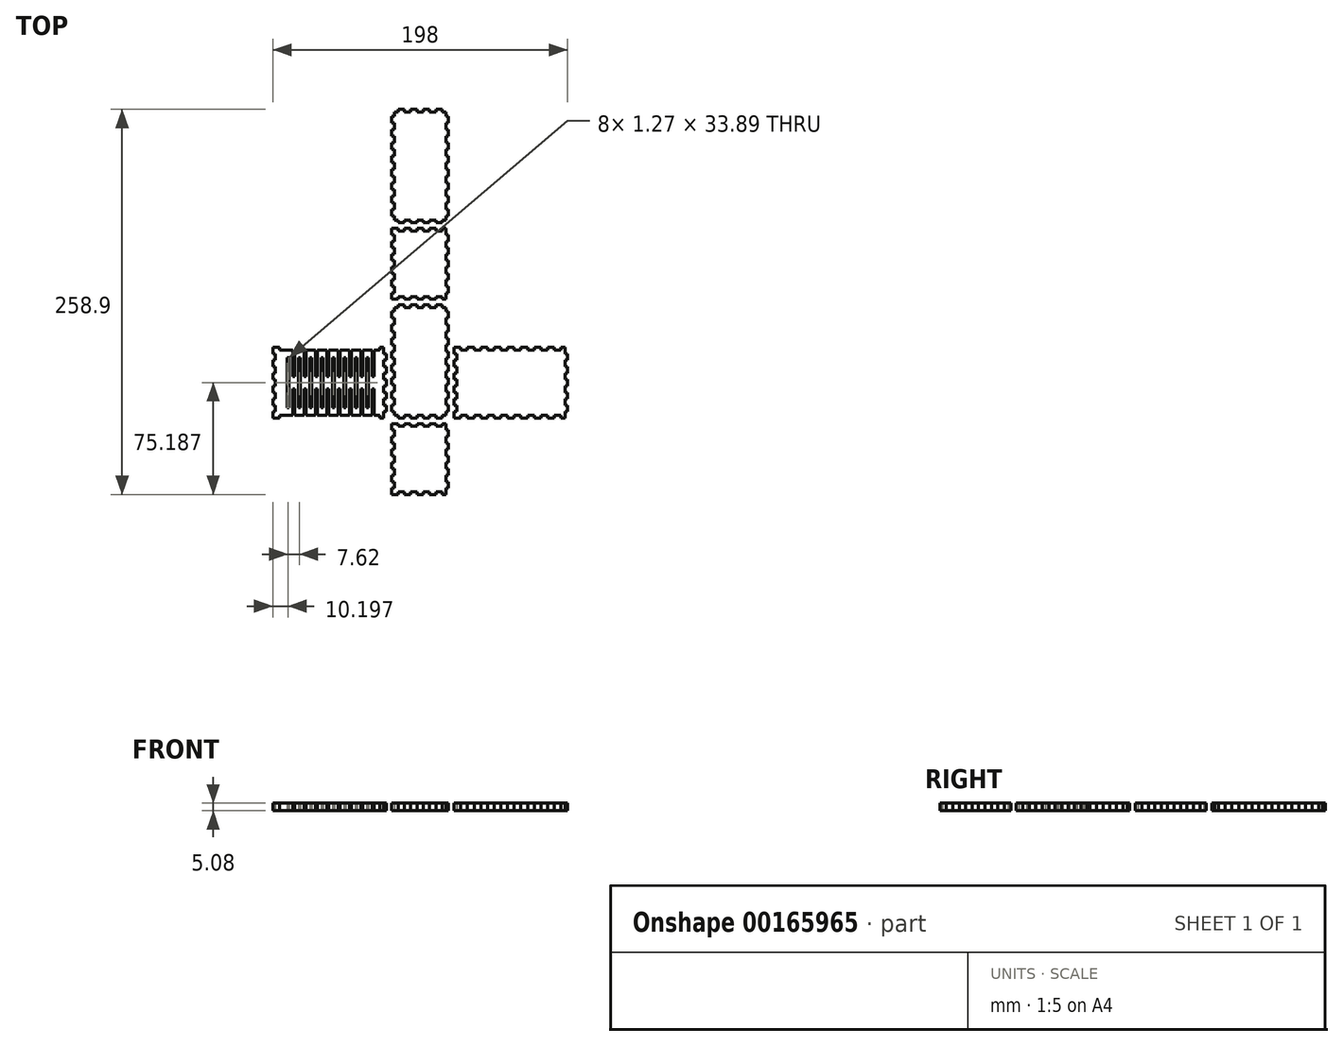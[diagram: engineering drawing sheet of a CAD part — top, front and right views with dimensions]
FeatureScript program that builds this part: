
annotation { "Feature Type Name" : "Feature", "Feature Type Description" : "" }
export const myFeature = defineFeature(function(context is Context, id is Id, definition is map)
    precondition{}
    {
        {
            var Q0;
            Q0=qCreatedBy(makeId("Top.planeOp"),FACE);
            var sketch = newSketch(context, id + "F0", { "sketchPlane" : qUnion([Q0])});
            skLineSegment(sketch, "E0", {"start": v(-19.05, -129.45) * mm, "end": v(-14.82, -129.45) * mm});
            skLineSegment(sketch, "E1", {"start": v(-14.82, -127.66) * mm, "end": v(-14.82, -129.45) * mm});
            skLineSegment(sketch, "E2", {"start": v(-14.82, -127.66) * mm, "end": v(-10.58, -127.66) * mm});
            skLineSegment(sketch, "E3", {"start": v(-10.58, -127.66) * mm, "end": v(-10.58, -129.45) * mm});
            skLineSegment(sketch, "E4", {"start": v(-10.58, -129.45) * mm, "end": v(-6.35, -129.45) * mm});
            skLineSegment(sketch, "E5", {"start": v(-6.35, -127.66) * mm, "end": v(-6.35, -129.45) * mm});
            skLineSegment(sketch, "E6", {"start": v(-6.35, -127.66) * mm, "end": v(-2.12, -127.66) * mm});
            skLineSegment(sketch, "E7", {"start": v(-2.12, -127.66) * mm, "end": v(-2.12, -129.45) * mm});
            skLineSegment(sketch, "E8", {"start": v(-2.12, -129.45) * mm, "end": v(2.12, -129.45) * mm});
            skLineSegment(sketch, "E9", {"start": v(2.12, -127.66) * mm, "end": v(2.12, -129.45) * mm});
            skLineSegment(sketch, "E10", {"start": v(2.12, -127.66) * mm, "end": v(6.35, -127.66) * mm});
            skLineSegment(sketch, "E11", {"start": v(6.35, -127.66) * mm, "end": v(6.35, -129.45) * mm});
            skLineSegment(sketch, "E12", {"start": v(6.35, -129.45) * mm, "end": v(10.58, -129.45) * mm});
            skLineSegment(sketch, "E13", {"start": v(10.58, -127.66) * mm, "end": v(10.58, -129.45) * mm});
            skLineSegment(sketch, "E14", {"start": v(10.58, -127.66) * mm, "end": v(14.82, -127.66) * mm});
            skLineSegment(sketch, "E15", {"start": v(14.82, -127.66) * mm, "end": v(14.82, -129.45) * mm});
            skLineSegment(sketch, "E16", {"start": v(14.82, -129.45) * mm, "end": v(17.26, -129.45) * mm});
            skLineSegment(sketch, "E17", {"start": v(-19.05, -81.83) * mm, "end": v(-14.82, -81.83) * mm});
            skLineSegment(sketch, "E18", {"start": v(-14.82, -81.83) * mm, "end": v(-14.82, -83.61) * mm});
            skLineSegment(sketch, "E19", {"start": v(-14.82, -83.61) * mm, "end": v(-10.58, -83.61) * mm});
            skLineSegment(sketch, "E20", {"start": v(-10.58, -81.83) * mm, "end": v(-10.58, -83.61) * mm});
            skLineSegment(sketch, "E21", {"start": v(-10.58, -81.83) * mm, "end": v(-6.35, -81.83) * mm});
            skLineSegment(sketch, "E22", {"start": v(-6.35, -81.83) * mm, "end": v(-6.35, -83.61) * mm});
            skLineSegment(sketch, "E23", {"start": v(-6.35, -83.61) * mm, "end": v(-2.12, -83.61) * mm});
            skLineSegment(sketch, "E24", {"start": v(-2.12, -81.83) * mm, "end": v(-2.12, -83.61) * mm});
            skLineSegment(sketch, "E25", {"start": v(-2.12, -81.83) * mm, "end": v(2.12, -81.83) * mm});
            skLineSegment(sketch, "E26", {"start": v(2.12, -81.83) * mm, "end": v(2.12, -83.61) * mm});
            skLineSegment(sketch, "E27", {"start": v(2.12, -83.61) * mm, "end": v(6.35, -83.61) * mm});
            skLineSegment(sketch, "E28", {"start": v(6.35, -81.83) * mm, "end": v(6.35, -83.61) * mm});
            skLineSegment(sketch, "E29", {"start": v(6.35, -81.83) * mm, "end": v(10.58, -81.83) * mm});
            skLineSegment(sketch, "E30", {"start": v(10.58, -81.83) * mm, "end": v(10.58, -83.61) * mm});
            skLineSegment(sketch, "E31", {"start": v(10.58, -83.61) * mm, "end": v(14.82, -83.61) * mm});
            skLineSegment(sketch, "E32", {"start": v(14.82, -81.83) * mm, "end": v(14.82, -83.61) * mm});
            skLineSegment(sketch, "E33", {"start": v(14.82, -81.83) * mm, "end": v(17.26, -81.83) * mm});
            skLineSegment(sketch, "E34", {"start": v(-19.05, -129.45) * mm, "end": v(-19.05, -125.12) * mm});
            skLineSegment(sketch, "E35", {"start": v(-17.26, -125.12) * mm, "end": v(-19.05, -125.12) * mm});
            skLineSegment(sketch, "E36", {"start": v(-17.26, -125.12) * mm, "end": v(-17.26, -120.8) * mm});
            skLineSegment(sketch, "E37", {"start": v(-17.26, -120.8) * mm, "end": v(-19.05, -120.8) * mm});
            skLineSegment(sketch, "E38", {"start": v(-19.05, -120.8) * mm, "end": v(-19.05, -116.46) * mm});
            skLineSegment(sketch, "E39", {"start": v(-17.26, -116.46) * mm, "end": v(-19.05, -116.46) * mm});
            skLineSegment(sketch, "E40", {"start": v(-17.26, -116.46) * mm, "end": v(-17.26, -112.13) * mm});
            skLineSegment(sketch, "E41", {"start": v(-17.26, -112.13) * mm, "end": v(-19.05, -112.13) * mm});
            skLineSegment(sketch, "E42", {"start": v(-19.05, -112.13) * mm, "end": v(-19.05, -107.8) * mm});
            skLineSegment(sketch, "E43", {"start": v(-17.26, -107.8) * mm, "end": v(-19.05, -107.8) * mm});
            skLineSegment(sketch, "E44", {"start": v(-17.26, -107.8) * mm, "end": v(-17.26, -103.47) * mm});
            skLineSegment(sketch, "E45", {"start": v(-17.26, -103.47) * mm, "end": v(-19.05, -103.47) * mm});
            skLineSegment(sketch, "E46", {"start": v(-19.05, -103.47) * mm, "end": v(-19.05, -99.14) * mm});
            skLineSegment(sketch, "E47", {"start": v(-17.26, -99.14) * mm, "end": v(-19.05, -99.14) * mm});
            skLineSegment(sketch, "E48", {"start": v(-17.26, -99.14) * mm, "end": v(-17.26, -94.81) * mm});
            skLineSegment(sketch, "E49", {"start": v(-17.26, -94.81) * mm, "end": v(-19.05, -94.81) * mm});
            skLineSegment(sketch, "E50", {"start": v(-19.05, -94.81) * mm, "end": v(-19.05, -90.48) * mm});
            skLineSegment(sketch, "E51", {"start": v(-17.26, -90.48) * mm, "end": v(-19.05, -90.48) * mm});
            skLineSegment(sketch, "E52", {"start": v(-17.26, -90.48) * mm, "end": v(-17.26, -86.15) * mm});
            skLineSegment(sketch, "E53", {"start": v(-17.26, -86.15) * mm, "end": v(-19.05, -86.15) * mm});
            skLineSegment(sketch, "E54", {"start": v(-19.05, -86.15) * mm, "end": v(-19.05, -81.83) * mm});
            skLineSegment(sketch, "E55", {"start": v(17.26, -129.45) * mm, "end": v(17.26, -125.12) * mm});
            skLineSegment(sketch, "E56", {"start": v(19.05, -125.12) * mm, "end": v(17.26, -125.12) * mm});
            skLineSegment(sketch, "E57", {"start": v(19.05, -125.12) * mm, "end": v(19.05, -120.8) * mm});
            skLineSegment(sketch, "E58", {"start": v(19.05, -120.8) * mm, "end": v(17.26, -120.8) * mm});
            skLineSegment(sketch, "E59", {"start": v(17.26, -120.8) * mm, "end": v(17.26, -116.46) * mm});
            skLineSegment(sketch, "E60", {"start": v(19.05, -116.46) * mm, "end": v(17.26, -116.46) * mm});
            skLineSegment(sketch, "E61", {"start": v(19.05, -116.46) * mm, "end": v(19.05, -112.13) * mm});
            skLineSegment(sketch, "E62", {"start": v(19.05, -112.13) * mm, "end": v(17.26, -112.13) * mm});
            skLineSegment(sketch, "E63", {"start": v(17.26, -112.13) * mm, "end": v(17.26, -107.8) * mm});
            skLineSegment(sketch, "E64", {"start": v(19.05, -107.8) * mm, "end": v(17.26, -107.8) * mm});
            skLineSegment(sketch, "E65", {"start": v(19.05, -107.8) * mm, "end": v(19.05, -103.47) * mm});
            skLineSegment(sketch, "E66", {"start": v(19.05, -103.47) * mm, "end": v(17.26, -103.47) * mm});
            skLineSegment(sketch, "E67", {"start": v(17.26, -103.47) * mm, "end": v(17.26, -99.14) * mm});
            skLineSegment(sketch, "E68", {"start": v(19.05, -99.14) * mm, "end": v(17.26, -99.14) * mm});
            skLineSegment(sketch, "E69", {"start": v(19.05, -99.14) * mm, "end": v(19.05, -94.81) * mm});
            skLineSegment(sketch, "E70", {"start": v(19.05, -94.81) * mm, "end": v(17.26, -94.81) * mm});
            skLineSegment(sketch, "E71", {"start": v(17.26, -94.81) * mm, "end": v(17.26, -90.48) * mm});
            skLineSegment(sketch, "E72", {"start": v(19.05, -90.48) * mm, "end": v(17.26, -90.48) * mm});
            skLineSegment(sketch, "E73", {"start": v(19.05, -90.48) * mm, "end": v(19.05, -86.15) * mm});
            skLineSegment(sketch, "E74", {"start": v(19.05, -86.15) * mm, "end": v(17.26, -86.15) * mm});
            skLineSegment(sketch, "E75", {"start": v(17.26, -86.15) * mm, "end": v(17.26, -81.83) * mm});
            skLineSegment(sketch, "E76", {"start": v(-99, -78.08) * mm, "end": v(-94.52, -78.08) * mm});
            skLineSegment(sketch, "E77", {"start": v(-94.52, -76.29) * mm, "end": v(-94.52, -78.08) * mm});
            skLineSegment(sketch, "E78", {"start": v(-94.52, -76.29) * mm, "end": v(-85.63, -76.29) * mm});
            skLineSegment(sketch, "E79", {"start": v(-27.28, -76.29) * mm, "end": v(-27.28, -78.08) * mm});
            skLineSegment(sketch, "E80", {"start": v(-27.28, -78.08) * mm, "end": v(-24.59, -78.08) * mm});
            skLineSegment(sketch, "E81", {"start": v(-99, -30.45) * mm, "end": v(-94.52, -30.45) * mm});
            skLineSegment(sketch, "E82", {"start": v(-94.52, -30.45) * mm, "end": v(-94.52, -32.24) * mm});
            skLineSegment(sketch, "E83", {"start": v(-27.28, -30.45) * mm, "end": v(-27.28, -32.24) * mm});
            skLineSegment(sketch, "E84", {"start": v(-27.28, -30.45) * mm, "end": v(-24.59, -30.45) * mm});
            skLineSegment(sketch, "E85", {"start": v(-99, -78.08) * mm, "end": v(-99, -73.75) * mm});
            skLineSegment(sketch, "E86", {"start": v(-97.21, -73.75) * mm, "end": v(-99, -73.75) * mm});
            skLineSegment(sketch, "E87", {"start": v(-97.21, -73.75) * mm, "end": v(-97.21, -69.42) * mm});
            skLineSegment(sketch, "E88", {"start": v(-97.21, -69.42) * mm, "end": v(-99, -69.42) * mm});
            skLineSegment(sketch, "E89", {"start": v(-99, -69.42) * mm, "end": v(-99, -65.09) * mm});
            skLineSegment(sketch, "E90", {"start": v(-97.21, -65.09) * mm, "end": v(-99, -65.09) * mm});
            skLineSegment(sketch, "E91", {"start": v(-97.21, -65.09) * mm, "end": v(-97.21, -60.76) * mm});
            skLineSegment(sketch, "E92", {"start": v(-97.21, -60.76) * mm, "end": v(-99, -60.76) * mm});
            skLineSegment(sketch, "E93", {"start": v(-99, -60.76) * mm, "end": v(-99, -56.43) * mm});
            skLineSegment(sketch, "E94", {"start": v(-97.21, -56.43) * mm, "end": v(-99, -56.43) * mm});
            skLineSegment(sketch, "E95", {"start": v(-97.21, -56.43) * mm, "end": v(-97.21, -52.1) * mm});
            skLineSegment(sketch, "E96", {"start": v(-97.21, -52.1) * mm, "end": v(-99, -52.1) * mm});
            skLineSegment(sketch, "E97", {"start": v(-99, -52.1) * mm, "end": v(-99, -47.77) * mm});
            skLineSegment(sketch, "E98", {"start": v(-97.21, -47.77) * mm, "end": v(-99, -47.77) * mm});
            skLineSegment(sketch, "E99", {"start": v(-97.21, -47.77) * mm, "end": v(-97.21, -43.44) * mm});
            skLineSegment(sketch, "E100", {"start": v(-97.21, -43.44) * mm, "end": v(-99, -43.44) * mm});
            skLineSegment(sketch, "E101", {"start": v(-99, -43.44) * mm, "end": v(-99, -39.1) * mm});
            skLineSegment(sketch, "E102", {"start": v(-97.21, -39.1) * mm, "end": v(-99, -39.1) * mm});
            skLineSegment(sketch, "E103", {"start": v(-97.21, -39.1) * mm, "end": v(-97.21, -34.78) * mm});
            skLineSegment(sketch, "E104", {"start": v(-97.21, -34.78) * mm, "end": v(-99, -34.78) * mm});
            skLineSegment(sketch, "E105", {"start": v(-99, -34.78) * mm, "end": v(-99, -30.45) * mm});
            skLineSegment(sketch, "E106", {"start": v(-24.59, -78.08) * mm, "end": v(-24.59, -73.75) * mm});
            skLineSegment(sketch, "E107", {"start": v(-22.8, -73.75) * mm, "end": v(-24.59, -73.75) * mm});
            skLineSegment(sketch, "E108", {"start": v(-22.8, -73.75) * mm, "end": v(-22.8, -69.42) * mm});
            skLineSegment(sketch, "E109", {"start": v(-22.8, -69.42) * mm, "end": v(-24.59, -69.42) * mm});
            skLineSegment(sketch, "E110", {"start": v(-24.59, -69.42) * mm, "end": v(-24.59, -65.09) * mm});
            skLineSegment(sketch, "E111", {"start": v(-22.8, -65.09) * mm, "end": v(-24.59, -65.09) * mm});
            skLineSegment(sketch, "E112", {"start": v(-22.8, -65.09) * mm, "end": v(-22.8, -60.76) * mm});
            skLineSegment(sketch, "E113", {"start": v(-22.8, -60.76) * mm, "end": v(-24.59, -60.76) * mm});
            skLineSegment(sketch, "E114", {"start": v(-24.59, -60.76) * mm, "end": v(-24.59, -56.43) * mm});
            skLineSegment(sketch, "E115", {"start": v(-22.8, -56.43) * mm, "end": v(-24.59, -56.43) * mm});
            skLineSegment(sketch, "E116", {"start": v(-22.8, -56.43) * mm, "end": v(-22.8, -52.1) * mm});
            skLineSegment(sketch, "E117", {"start": v(-22.8, -52.1) * mm, "end": v(-24.59, -52.1) * mm});
            skLineSegment(sketch, "E118", {"start": v(-24.59, -52.1) * mm, "end": v(-24.59, -47.77) * mm});
            skLineSegment(sketch, "E119", {"start": v(-22.8, -47.77) * mm, "end": v(-24.59, -47.77) * mm});
            skLineSegment(sketch, "E120", {"start": v(-22.8, -47.77) * mm, "end": v(-22.8, -43.44) * mm});
            skLineSegment(sketch, "E121", {"start": v(-22.8, -43.44) * mm, "end": v(-24.59, -43.44) * mm});
            skLineSegment(sketch, "E122", {"start": v(-24.59, -43.44) * mm, "end": v(-24.59, -39.1) * mm});
            skLineSegment(sketch, "E123", {"start": v(-22.8, -39.1) * mm, "end": v(-24.59, -39.1) * mm});
            skLineSegment(sketch, "E124", {"start": v(-22.8, -39.1) * mm, "end": v(-22.8, -34.78) * mm});
            skLineSegment(sketch, "E125", {"start": v(-22.8, -34.78) * mm, "end": v(-24.59, -34.78) * mm});
            skLineSegment(sketch, "E126", {"start": v(-24.59, -34.78) * mm, "end": v(-24.59, -30.45) * mm});
            skLineSegment(sketch, "E127", {"start": v(-17.26, -76.29) * mm, "end": v(-14.82, -76.29) * mm});
            skLineSegment(sketch, "E128", {"start": v(-14.82, -76.29) * mm, "end": v(-14.82, -78.08) * mm});
            skLineSegment(sketch, "E129", {"start": v(-14.82, -78.08) * mm, "end": v(-10.58, -78.08) * mm});
            skLineSegment(sketch, "E130", {"start": v(-10.58, -76.29) * mm, "end": v(-10.58, -78.08) * mm});
            skLineSegment(sketch, "E131", {"start": v(-10.58, -76.29) * mm, "end": v(-6.35, -76.29) * mm});
            skLineSegment(sketch, "E132", {"start": v(-6.35, -76.29) * mm, "end": v(-6.35, -78.08) * mm});
            skLineSegment(sketch, "E133", {"start": v(-6.35, -78.08) * mm, "end": v(-2.12, -78.08) * mm});
            skLineSegment(sketch, "E134", {"start": v(-2.12, -76.29) * mm, "end": v(-2.12, -78.08) * mm});
            skLineSegment(sketch, "E135", {"start": v(-2.12, -76.29) * mm, "end": v(2.12, -76.29) * mm});
            skLineSegment(sketch, "E136", {"start": v(2.12, -76.29) * mm, "end": v(2.12, -78.08) * mm});
            skLineSegment(sketch, "E137", {"start": v(2.12, -78.08) * mm, "end": v(6.35, -78.08) * mm});
            skLineSegment(sketch, "E138", {"start": v(6.35, -76.29) * mm, "end": v(6.35, -78.08) * mm});
            skLineSegment(sketch, "E139", {"start": v(6.35, -76.29) * mm, "end": v(10.58, -76.29) * mm});
            skLineSegment(sketch, "E140", {"start": v(10.58, -76.29) * mm, "end": v(10.58, -78.08) * mm});
            skLineSegment(sketch, "E141", {"start": v(10.58, -78.08) * mm, "end": v(14.82, -78.08) * mm});
            skLineSegment(sketch, "E142", {"start": v(14.82, -76.29) * mm, "end": v(14.82, -78.08) * mm});
            skLineSegment(sketch, "E143", {"start": v(14.82, -76.29) * mm, "end": v(17.26, -76.29) * mm});
            skLineSegment(sketch, "E144", {"start": v(-17.26, -3.66) * mm, "end": v(-14.82, -3.66) * mm});
            skLineSegment(sketch, "E145", {"start": v(-14.82, -1.88) * mm, "end": v(-14.82, -3.66) * mm});
            skLineSegment(sketch, "E146", {"start": v(-14.82, -1.88) * mm, "end": v(-10.58, -1.88) * mm});
            skLineSegment(sketch, "E147", {"start": v(-10.58, -1.88) * mm, "end": v(-10.58, -3.66) * mm});
            skLineSegment(sketch, "E148", {"start": v(-10.58, -3.66) * mm, "end": v(-6.35, -3.66) * mm});
            skLineSegment(sketch, "E149", {"start": v(-6.35, -1.88) * mm, "end": v(-6.35, -3.66) * mm});
            skLineSegment(sketch, "E150", {"start": v(-6.35, -1.88) * mm, "end": v(-2.12, -1.88) * mm});
            skLineSegment(sketch, "E151", {"start": v(-2.12, -1.88) * mm, "end": v(-2.12, -3.66) * mm});
            skLineSegment(sketch, "E152", {"start": v(-2.12, -3.66) * mm, "end": v(2.12, -3.66) * mm});
            skLineSegment(sketch, "E153", {"start": v(2.12, -1.88) * mm, "end": v(2.12, -3.66) * mm});
            skLineSegment(sketch, "E154", {"start": v(2.12, -1.88) * mm, "end": v(6.35, -1.88) * mm});
            skLineSegment(sketch, "E155", {"start": v(6.35, -1.88) * mm, "end": v(6.35, -3.66) * mm});
            skLineSegment(sketch, "E156", {"start": v(6.35, -3.66) * mm, "end": v(10.58, -3.66) * mm});
            skLineSegment(sketch, "E157", {"start": v(10.58, -1.88) * mm, "end": v(10.58, -3.66) * mm});
            skLineSegment(sketch, "E158", {"start": v(10.58, -1.88) * mm, "end": v(14.82, -1.88) * mm});
            skLineSegment(sketch, "E159", {"start": v(14.82, -1.88) * mm, "end": v(14.82, -3.66) * mm});
            skLineSegment(sketch, "E160", {"start": v(14.82, -3.66) * mm, "end": v(17.26, -3.66) * mm});
            skLineSegment(sketch, "E161", {"start": v(-17.26, -76.29) * mm, "end": v(-17.26, -73.6) * mm});
            skLineSegment(sketch, "E162", {"start": v(-17.26, -73.6) * mm, "end": v(-19.05, -73.6) * mm});
            skLineSegment(sketch, "E163", {"start": v(-19.05, -73.6) * mm, "end": v(-19.05, -69.11) * mm});
            skLineSegment(sketch, "E164", {"start": v(-17.26, -69.11) * mm, "end": v(-19.05, -69.11) * mm});
            skLineSegment(sketch, "E165", {"start": v(-17.26, -69.11) * mm, "end": v(-17.26, -64.63) * mm});
            skLineSegment(sketch, "E166", {"start": v(-17.26, -64.63) * mm, "end": v(-19.05, -64.63) * mm});
            skLineSegment(sketch, "E167", {"start": v(-19.05, -64.63) * mm, "end": v(-19.05, -60.15) * mm});
            skLineSegment(sketch, "E168", {"start": v(-17.26, -60.15) * mm, "end": v(-19.05, -60.15) * mm});
            skLineSegment(sketch, "E169", {"start": v(-17.26, -60.15) * mm, "end": v(-17.26, -55.66) * mm});
            skLineSegment(sketch, "E170", {"start": v(-17.26, -55.66) * mm, "end": v(-19.05, -55.66) * mm});
            skLineSegment(sketch, "E171", {"start": v(-19.05, -55.66) * mm, "end": v(-19.05, -51.18) * mm});
            skLineSegment(sketch, "E172", {"start": v(-17.26, -51.18) * mm, "end": v(-19.05, -51.18) * mm});
            skLineSegment(sketch, "E173", {"start": v(-17.26, -51.18) * mm, "end": v(-17.26, -46.7) * mm});
            skLineSegment(sketch, "E174", {"start": v(-17.26, -46.7) * mm, "end": v(-19.05, -46.7) * mm});
            skLineSegment(sketch, "E175", {"start": v(-19.05, -46.7) * mm, "end": v(-19.05, -42.22) * mm});
            skLineSegment(sketch, "E176", {"start": v(-17.26, -42.22) * mm, "end": v(-19.05, -42.22) * mm});
            skLineSegment(sketch, "E177", {"start": v(-17.26, -42.22) * mm, "end": v(-17.26, -37.73) * mm});
            skLineSegment(sketch, "E178", {"start": v(-17.26, -37.73) * mm, "end": v(-19.05, -37.73) * mm});
            skLineSegment(sketch, "E179", {"start": v(-19.05, -37.73) * mm, "end": v(-19.05, -33.25) * mm});
            skLineSegment(sketch, "E180", {"start": v(-17.26, -33.25) * mm, "end": v(-19.05, -33.25) * mm});
            skLineSegment(sketch, "E181", {"start": v(-17.26, -33.25) * mm, "end": v(-17.26, -28.77) * mm});
            skLineSegment(sketch, "E182", {"start": v(-17.26, -28.77) * mm, "end": v(-19.05, -28.77) * mm});
            skLineSegment(sketch, "E183", {"start": v(-19.05, -28.77) * mm, "end": v(-19.05, -24.29) * mm});
            skLineSegment(sketch, "E184", {"start": v(-17.26, -24.29) * mm, "end": v(-19.05, -24.29) * mm});
            skLineSegment(sketch, "E185", {"start": v(-17.26, -24.29) * mm, "end": v(-17.26, -19.8) * mm});
            skLineSegment(sketch, "E186", {"start": v(-17.26, -19.8) * mm, "end": v(-19.05, -19.8) * mm});
            skLineSegment(sketch, "E187", {"start": v(-19.05, -19.8) * mm, "end": v(-19.05, -15.32) * mm});
            skLineSegment(sketch, "E188", {"start": v(-17.26, -15.32) * mm, "end": v(-19.05, -15.32) * mm});
            skLineSegment(sketch, "E189", {"start": v(-17.26, -15.32) * mm, "end": v(-17.26, -10.84) * mm});
            skLineSegment(sketch, "E190", {"start": v(-17.26, -10.84) * mm, "end": v(-19.05, -10.84) * mm});
            skLineSegment(sketch, "E191", {"start": v(-19.05, -10.84) * mm, "end": v(-19.05, -6.36) * mm});
            skLineSegment(sketch, "E192", {"start": v(-17.26, -6.36) * mm, "end": v(-19.05, -6.36) * mm});
            skLineSegment(sketch, "E193", {"start": v(-17.26, -6.36) * mm, "end": v(-17.26, -3.66) * mm});
            skLineSegment(sketch, "E194", {"start": v(17.26, -76.29) * mm, "end": v(17.26, -73.6) * mm});
            skLineSegment(sketch, "E195", {"start": v(19.05, -73.6) * mm, "end": v(17.26, -73.6) * mm});
            skLineSegment(sketch, "E196", {"start": v(19.05, -73.6) * mm, "end": v(19.05, -69.11) * mm});
            skLineSegment(sketch, "E197", {"start": v(19.05, -69.11) * mm, "end": v(17.26, -69.11) * mm});
            skLineSegment(sketch, "E198", {"start": v(17.26, -69.11) * mm, "end": v(17.26, -64.63) * mm});
            skLineSegment(sketch, "E199", {"start": v(19.05, -64.63) * mm, "end": v(17.26, -64.63) * mm});
            skLineSegment(sketch, "E200", {"start": v(19.05, -64.63) * mm, "end": v(19.05, -60.15) * mm});
            skLineSegment(sketch, "E201", {"start": v(19.05, -60.15) * mm, "end": v(17.26, -60.15) * mm});
            skLineSegment(sketch, "E202", {"start": v(17.26, -60.15) * mm, "end": v(17.26, -55.66) * mm});
            skLineSegment(sketch, "E203", {"start": v(19.05, -55.66) * mm, "end": v(17.26, -55.66) * mm});
            skLineSegment(sketch, "E204", {"start": v(19.05, -55.66) * mm, "end": v(19.05, -51.18) * mm});
            skLineSegment(sketch, "E205", {"start": v(19.05, -51.18) * mm, "end": v(17.26, -51.18) * mm});
            skLineSegment(sketch, "E206", {"start": v(17.26, -51.18) * mm, "end": v(17.26, -46.7) * mm});
            skLineSegment(sketch, "E207", {"start": v(19.05, -46.7) * mm, "end": v(17.26, -46.7) * mm});
            skLineSegment(sketch, "E208", {"start": v(19.05, -46.7) * mm, "end": v(19.05, -42.22) * mm});
            skLineSegment(sketch, "E209", {"start": v(19.05, -42.22) * mm, "end": v(17.26, -42.22) * mm});
            skLineSegment(sketch, "E210", {"start": v(17.26, -42.22) * mm, "end": v(17.26, -37.73) * mm});
            skLineSegment(sketch, "E211", {"start": v(19.05, -37.73) * mm, "end": v(17.26, -37.73) * mm});
            skLineSegment(sketch, "E212", {"start": v(19.05, -37.73) * mm, "end": v(19.05, -33.25) * mm});
            skLineSegment(sketch, "E213", {"start": v(19.05, -33.25) * mm, "end": v(17.26, -33.25) * mm});
            skLineSegment(sketch, "E214", {"start": v(17.26, -33.25) * mm, "end": v(17.26, -28.77) * mm});
            skLineSegment(sketch, "E215", {"start": v(19.05, -28.77) * mm, "end": v(17.26, -28.77) * mm});
            skLineSegment(sketch, "E216", {"start": v(19.05, -28.77) * mm, "end": v(19.05, -24.29) * mm});
            skLineSegment(sketch, "E217", {"start": v(19.05, -24.29) * mm, "end": v(17.26, -24.29) * mm});
            skLineSegment(sketch, "E218", {"start": v(17.26, -24.29) * mm, "end": v(17.26, -19.8) * mm});
            skLineSegment(sketch, "E219", {"start": v(19.05, -19.8) * mm, "end": v(17.26, -19.8) * mm});
            skLineSegment(sketch, "E220", {"start": v(19.05, -19.8) * mm, "end": v(19.05, -15.32) * mm});
            skLineSegment(sketch, "E221", {"start": v(19.05, -15.32) * mm, "end": v(17.26, -15.32) * mm});
            skLineSegment(sketch, "E222", {"start": v(17.26, -15.32) * mm, "end": v(17.26, -10.84) * mm});
            skLineSegment(sketch, "E223", {"start": v(19.05, -10.84) * mm, "end": v(17.26, -10.84) * mm});
            skLineSegment(sketch, "E224", {"start": v(19.05, -10.84) * mm, "end": v(19.05, -6.36) * mm});
            skLineSegment(sketch, "E225", {"start": v(19.05, -6.36) * mm, "end": v(17.26, -6.36) * mm});
            skLineSegment(sketch, "E226", {"start": v(17.26, -6.36) * mm, "end": v(17.26, -3.66) * mm});
            skLineSegment(sketch, "E227", {"start": v(22.8, -78.08) * mm, "end": v(27.28, -78.08) * mm});
            skLineSegment(sketch, "E228", {"start": v(27.28, -76.29) * mm, "end": v(27.28, -78.08) * mm});
            skLineSegment(sketch, "E229", {"start": v(27.28, -76.29) * mm, "end": v(31.76, -76.29) * mm});
            skLineSegment(sketch, "E230", {"start": v(31.76, -76.29) * mm, "end": v(31.76, -78.08) * mm});
            skLineSegment(sketch, "E231", {"start": v(31.76, -78.08) * mm, "end": v(36.25, -78.08) * mm});
            skLineSegment(sketch, "E232", {"start": v(36.25, -76.29) * mm, "end": v(36.25, -78.08) * mm});
            skLineSegment(sketch, "E233", {"start": v(36.25, -76.29) * mm, "end": v(40.73, -76.29) * mm});
            skLineSegment(sketch, "E234", {"start": v(40.73, -76.29) * mm, "end": v(40.73, -78.08) * mm});
            skLineSegment(sketch, "E235", {"start": v(40.73, -78.08) * mm, "end": v(45.21, -78.08) * mm});
            skLineSegment(sketch, "E236", {"start": v(45.21, -76.29) * mm, "end": v(45.21, -78.08) * mm});
            skLineSegment(sketch, "E237", {"start": v(45.21, -76.29) * mm, "end": v(49.7, -76.29) * mm});
            skLineSegment(sketch, "E238", {"start": v(49.7, -76.29) * mm, "end": v(49.7, -78.08) * mm});
            skLineSegment(sketch, "E239", {"start": v(49.7, -78.08) * mm, "end": v(54.18, -78.08) * mm});
            skLineSegment(sketch, "E240", {"start": v(54.18, -76.29) * mm, "end": v(54.18, -78.08) * mm});
            skLineSegment(sketch, "E241", {"start": v(54.18, -76.29) * mm, "end": v(58.66, -76.29) * mm});
            skLineSegment(sketch, "E242", {"start": v(58.66, -76.29) * mm, "end": v(58.66, -78.08) * mm});
            skLineSegment(sketch, "E243", {"start": v(58.66, -78.08) * mm, "end": v(63.14, -78.08) * mm});
            skLineSegment(sketch, "E244", {"start": v(63.14, -76.29) * mm, "end": v(63.14, -78.08) * mm});
            skLineSegment(sketch, "E245", {"start": v(63.14, -76.29) * mm, "end": v(67.62, -76.29) * mm});
            skLineSegment(sketch, "E246", {"start": v(67.62, -76.29) * mm, "end": v(67.62, -78.08) * mm});
            skLineSegment(sketch, "E247", {"start": v(67.62, -78.08) * mm, "end": v(72.1, -78.08) * mm});
            skLineSegment(sketch, "E248", {"start": v(72.1, -76.29) * mm, "end": v(72.1, -78.08) * mm});
            skLineSegment(sketch, "E249", {"start": v(72.1, -76.29) * mm, "end": v(76.59, -76.29) * mm});
            skLineSegment(sketch, "E250", {"start": v(76.59, -76.29) * mm, "end": v(76.59, -78.08) * mm});
            skLineSegment(sketch, "E251", {"start": v(76.59, -78.08) * mm, "end": v(81.07, -78.08) * mm});
            skLineSegment(sketch, "E252", {"start": v(81.07, -76.29) * mm, "end": v(81.07, -78.08) * mm});
            skLineSegment(sketch, "E253", {"start": v(81.07, -76.29) * mm, "end": v(85.55, -76.29) * mm});
            skLineSegment(sketch, "E254", {"start": v(85.55, -76.29) * mm, "end": v(85.55, -78.08) * mm});
            skLineSegment(sketch, "E255", {"start": v(85.55, -78.08) * mm, "end": v(90.04, -78.08) * mm});
            skLineSegment(sketch, "E256", {"start": v(90.04, -76.29) * mm, "end": v(90.04, -78.08) * mm});
            skLineSegment(sketch, "E257", {"start": v(90.04, -76.29) * mm, "end": v(94.52, -76.29) * mm});
            skLineSegment(sketch, "E258", {"start": v(94.52, -76.29) * mm, "end": v(94.52, -78.08) * mm});
            skLineSegment(sketch, "E259", {"start": v(94.52, -78.08) * mm, "end": v(97.21, -78.08) * mm});
            skLineSegment(sketch, "E260", {"start": v(22.8, -30.45) * mm, "end": v(27.28, -30.45) * mm});
            skLineSegment(sketch, "E261", {"start": v(27.28, -30.45) * mm, "end": v(27.28, -32.24) * mm});
            skLineSegment(sketch, "E262", {"start": v(27.28, -32.24) * mm, "end": v(31.76, -32.24) * mm});
            skLineSegment(sketch, "E263", {"start": v(31.76, -30.45) * mm, "end": v(31.76, -32.24) * mm});
            skLineSegment(sketch, "E264", {"start": v(31.76, -30.45) * mm, "end": v(36.25, -30.45) * mm});
            skLineSegment(sketch, "E265", {"start": v(36.25, -30.45) * mm, "end": v(36.25, -32.24) * mm});
            skLineSegment(sketch, "E266", {"start": v(36.25, -32.24) * mm, "end": v(40.73, -32.24) * mm});
            skLineSegment(sketch, "E267", {"start": v(40.73, -30.45) * mm, "end": v(40.73, -32.24) * mm});
            skLineSegment(sketch, "E268", {"start": v(40.73, -30.45) * mm, "end": v(45.21, -30.45) * mm});
            skLineSegment(sketch, "E269", {"start": v(45.21, -30.45) * mm, "end": v(45.21, -32.24) * mm});
            skLineSegment(sketch, "E270", {"start": v(45.21, -32.24) * mm, "end": v(49.7, -32.24) * mm});
            skLineSegment(sketch, "E271", {"start": v(49.7, -30.45) * mm, "end": v(49.7, -32.24) * mm});
            skLineSegment(sketch, "E272", {"start": v(49.7, -30.45) * mm, "end": v(54.18, -30.45) * mm});
            skLineSegment(sketch, "E273", {"start": v(54.18, -30.45) * mm, "end": v(54.18, -32.24) * mm});
            skLineSegment(sketch, "E274", {"start": v(54.18, -32.24) * mm, "end": v(58.66, -32.24) * mm});
            skLineSegment(sketch, "E275", {"start": v(58.66, -30.45) * mm, "end": v(58.66, -32.24) * mm});
            skLineSegment(sketch, "E276", {"start": v(58.66, -30.45) * mm, "end": v(63.14, -30.45) * mm});
            skLineSegment(sketch, "E277", {"start": v(63.14, -30.45) * mm, "end": v(63.14, -32.24) * mm});
            skLineSegment(sketch, "E278", {"start": v(63.14, -32.24) * mm, "end": v(67.62, -32.24) * mm});
            skLineSegment(sketch, "E279", {"start": v(67.62, -30.45) * mm, "end": v(67.62, -32.24) * mm});
            skLineSegment(sketch, "E280", {"start": v(67.62, -30.45) * mm, "end": v(72.1, -30.45) * mm});
            skLineSegment(sketch, "E281", {"start": v(72.1, -30.45) * mm, "end": v(72.1, -32.24) * mm});
            skLineSegment(sketch, "E282", {"start": v(72.1, -32.24) * mm, "end": v(76.59, -32.24) * mm});
            skLineSegment(sketch, "E283", {"start": v(76.59, -30.45) * mm, "end": v(76.59, -32.24) * mm});
            skLineSegment(sketch, "E284", {"start": v(76.59, -30.45) * mm, "end": v(81.07, -30.45) * mm});
            skLineSegment(sketch, "E285", {"start": v(81.07, -30.45) * mm, "end": v(81.07, -32.24) * mm});
            skLineSegment(sketch, "E286", {"start": v(81.07, -32.24) * mm, "end": v(85.55, -32.24) * mm});
            skLineSegment(sketch, "E287", {"start": v(85.55, -30.45) * mm, "end": v(85.55, -32.24) * mm});
            skLineSegment(sketch, "E288", {"start": v(85.55, -30.45) * mm, "end": v(90.04, -30.45) * mm});
            skLineSegment(sketch, "E289", {"start": v(90.04, -30.45) * mm, "end": v(90.04, -32.24) * mm});
            skLineSegment(sketch, "E290", {"start": v(90.04, -32.24) * mm, "end": v(94.52, -32.24) * mm});
            skLineSegment(sketch, "E291", {"start": v(94.52, -30.45) * mm, "end": v(94.52, -32.24) * mm});
            skLineSegment(sketch, "E292", {"start": v(94.52, -30.45) * mm, "end": v(97.21, -30.45) * mm});
            skLineSegment(sketch, "E293", {"start": v(22.8, -78.08) * mm, "end": v(22.8, -73.75) * mm});
            skLineSegment(sketch, "E294", {"start": v(24.59, -73.75) * mm, "end": v(22.8, -73.75) * mm});
            skLineSegment(sketch, "E295", {"start": v(24.59, -73.75) * mm, "end": v(24.59, -69.42) * mm});
            skLineSegment(sketch, "E296", {"start": v(24.59, -69.42) * mm, "end": v(22.8, -69.42) * mm});
            skLineSegment(sketch, "E297", {"start": v(22.8, -69.42) * mm, "end": v(22.8, -65.09) * mm});
            skLineSegment(sketch, "E298", {"start": v(24.59, -65.09) * mm, "end": v(22.8, -65.09) * mm});
            skLineSegment(sketch, "E299", {"start": v(24.59, -65.09) * mm, "end": v(24.59, -60.76) * mm});
            skLineSegment(sketch, "E300", {"start": v(24.59, -60.76) * mm, "end": v(22.8, -60.76) * mm});
            skLineSegment(sketch, "E301", {"start": v(22.8, -60.76) * mm, "end": v(22.8, -56.43) * mm});
            skLineSegment(sketch, "E302", {"start": v(24.59, -56.43) * mm, "end": v(22.8, -56.43) * mm});
            skLineSegment(sketch, "E303", {"start": v(24.59, -56.43) * mm, "end": v(24.59, -52.1) * mm});
            skLineSegment(sketch, "E304", {"start": v(24.59, -52.1) * mm, "end": v(22.8, -52.1) * mm});
            skLineSegment(sketch, "E305", {"start": v(22.8, -52.1) * mm, "end": v(22.8, -47.77) * mm});
            skLineSegment(sketch, "E306", {"start": v(24.59, -47.77) * mm, "end": v(22.8, -47.77) * mm});
            skLineSegment(sketch, "E307", {"start": v(24.59, -47.77) * mm, "end": v(24.59, -43.44) * mm});
            skLineSegment(sketch, "E308", {"start": v(24.59, -43.44) * mm, "end": v(22.8, -43.44) * mm});
            skLineSegment(sketch, "E309", {"start": v(22.8, -43.44) * mm, "end": v(22.8, -39.1) * mm});
            skLineSegment(sketch, "E310", {"start": v(24.59, -39.1) * mm, "end": v(22.8, -39.1) * mm});
            skLineSegment(sketch, "E311", {"start": v(24.59, -39.1) * mm, "end": v(24.59, -34.78) * mm});
            skLineSegment(sketch, "E312", {"start": v(24.59, -34.78) * mm, "end": v(22.8, -34.78) * mm});
            skLineSegment(sketch, "E313", {"start": v(22.8, -34.78) * mm, "end": v(22.8, -30.45) * mm});
            skLineSegment(sketch, "E314", {"start": v(97.21, -78.08) * mm, "end": v(97.21, -73.75) * mm});
            skLineSegment(sketch, "E315", {"start": v(99, -73.75) * mm, "end": v(97.21, -73.75) * mm});
            skLineSegment(sketch, "E316", {"start": v(99, -73.75) * mm, "end": v(99, -69.42) * mm});
            skLineSegment(sketch, "E317", {"start": v(99, -69.42) * mm, "end": v(97.21, -69.42) * mm});
            skLineSegment(sketch, "E318", {"start": v(97.21, -69.42) * mm, "end": v(97.21, -65.09) * mm});
            skLineSegment(sketch, "E319", {"start": v(99, -65.09) * mm, "end": v(97.21, -65.09) * mm});
            skLineSegment(sketch, "E320", {"start": v(99, -65.09) * mm, "end": v(99, -60.76) * mm});
            skLineSegment(sketch, "E321", {"start": v(99, -60.76) * mm, "end": v(97.21, -60.76) * mm});
            skLineSegment(sketch, "E322", {"start": v(97.21, -60.76) * mm, "end": v(97.21, -56.43) * mm});
            skLineSegment(sketch, "E323", {"start": v(99, -56.43) * mm, "end": v(97.21, -56.43) * mm});
            skLineSegment(sketch, "E324", {"start": v(99, -56.43) * mm, "end": v(99, -52.1) * mm});
            skLineSegment(sketch, "E325", {"start": v(99, -52.1) * mm, "end": v(97.21, -52.1) * mm});
            skLineSegment(sketch, "E326", {"start": v(97.21, -52.1) * mm, "end": v(97.21, -47.77) * mm});
            skLineSegment(sketch, "E327", {"start": v(99, -47.77) * mm, "end": v(97.21, -47.77) * mm});
            skLineSegment(sketch, "E328", {"start": v(99, -47.77) * mm, "end": v(99, -43.44) * mm});
            skLineSegment(sketch, "E329", {"start": v(99, -43.44) * mm, "end": v(97.21, -43.44) * mm});
            skLineSegment(sketch, "E330", {"start": v(97.21, -43.44) * mm, "end": v(97.21, -39.1) * mm});
            skLineSegment(sketch, "E331", {"start": v(99, -39.1) * mm, "end": v(97.21, -39.1) * mm});
            skLineSegment(sketch, "E332", {"start": v(99, -39.1) * mm, "end": v(99, -34.78) * mm});
            skLineSegment(sketch, "E333", {"start": v(99, -34.78) * mm, "end": v(97.21, -34.78) * mm});
            skLineSegment(sketch, "E334", {"start": v(97.21, -34.78) * mm, "end": v(97.21, -30.45) * mm});
            skLineSegment(sketch, "E335", {"start": v(-19.05, 1.87) * mm, "end": v(-14.82, 1.87) * mm});
            skLineSegment(sketch, "E336", {"start": v(-14.82, 3.66) * mm, "end": v(-14.82, 1.87) * mm});
            skLineSegment(sketch, "E337", {"start": v(-14.82, 3.66) * mm, "end": v(-10.58, 3.66) * mm});
            skLineSegment(sketch, "E338", {"start": v(-10.58, 3.66) * mm, "end": v(-10.58, 1.87) * mm});
            skLineSegment(sketch, "E339", {"start": v(-10.58, 1.87) * mm, "end": v(-6.35, 1.87) * mm});
            skLineSegment(sketch, "E340", {"start": v(-6.35, 3.66) * mm, "end": v(-6.35, 1.87) * mm});
            skLineSegment(sketch, "E341", {"start": v(-6.35, 3.66) * mm, "end": v(-2.12, 3.66) * mm});
            skLineSegment(sketch, "E342", {"start": v(-2.12, 3.66) * mm, "end": v(-2.12, 1.87) * mm});
            skLineSegment(sketch, "E343", {"start": v(-2.12, 1.87) * mm, "end": v(2.12, 1.87) * mm});
            skLineSegment(sketch, "E344", {"start": v(2.12, 3.66) * mm, "end": v(2.12, 1.87) * mm});
            skLineSegment(sketch, "E345", {"start": v(2.12, 3.66) * mm, "end": v(6.35, 3.66) * mm});
            skLineSegment(sketch, "E346", {"start": v(6.35, 3.66) * mm, "end": v(6.35, 1.87) * mm});
            skLineSegment(sketch, "E347", {"start": v(6.35, 1.87) * mm, "end": v(10.58, 1.87) * mm});
            skLineSegment(sketch, "E348", {"start": v(10.58, 3.66) * mm, "end": v(10.58, 1.87) * mm});
            skLineSegment(sketch, "E349", {"start": v(10.58, 3.66) * mm, "end": v(14.82, 3.66) * mm});
            skLineSegment(sketch, "E350", {"start": v(14.82, 3.66) * mm, "end": v(14.82, 1.87) * mm});
            skLineSegment(sketch, "E351", {"start": v(14.82, 1.87) * mm, "end": v(17.26, 1.87) * mm});
            skLineSegment(sketch, "E352", {"start": v(-19.05, 49.5) * mm, "end": v(-14.82, 49.5) * mm});
            skLineSegment(sketch, "E353", {"start": v(-14.82, 49.5) * mm, "end": v(-14.82, 47.71) * mm});
            skLineSegment(sketch, "E354", {"start": v(-14.82, 47.71) * mm, "end": v(-10.58, 47.71) * mm});
            skLineSegment(sketch, "E355", {"start": v(-10.58, 49.5) * mm, "end": v(-10.58, 47.71) * mm});
            skLineSegment(sketch, "E356", {"start": v(-10.58, 49.5) * mm, "end": v(-6.35, 49.5) * mm});
            skLineSegment(sketch, "E357", {"start": v(-6.35, 49.5) * mm, "end": v(-6.35, 47.71) * mm});
            skLineSegment(sketch, "E358", {"start": v(-6.35, 47.71) * mm, "end": v(-2.12, 47.71) * mm});
            skLineSegment(sketch, "E359", {"start": v(-2.12, 49.5) * mm, "end": v(-2.12, 47.71) * mm});
            skLineSegment(sketch, "E360", {"start": v(-2.12, 49.5) * mm, "end": v(2.12, 49.5) * mm});
            skLineSegment(sketch, "E361", {"start": v(2.12, 49.5) * mm, "end": v(2.12, 47.71) * mm});
            skLineSegment(sketch, "E362", {"start": v(2.12, 47.71) * mm, "end": v(6.35, 47.71) * mm});
            skLineSegment(sketch, "E363", {"start": v(6.35, 49.5) * mm, "end": v(6.35, 47.71) * mm});
            skLineSegment(sketch, "E364", {"start": v(6.35, 49.5) * mm, "end": v(10.58, 49.5) * mm});
            skLineSegment(sketch, "E365", {"start": v(10.58, 49.5) * mm, "end": v(10.58, 47.71) * mm});
            skLineSegment(sketch, "E366", {"start": v(10.58, 47.71) * mm, "end": v(14.82, 47.71) * mm});
            skLineSegment(sketch, "E367", {"start": v(14.82, 49.5) * mm, "end": v(14.82, 47.71) * mm});
            skLineSegment(sketch, "E368", {"start": v(14.82, 49.5) * mm, "end": v(17.26, 49.5) * mm});
            skLineSegment(sketch, "E369", {"start": v(-19.05, 1.87) * mm, "end": v(-19.05, 6.2) * mm});
            skLineSegment(sketch, "E370", {"start": v(-17.26, 6.2) * mm, "end": v(-19.05, 6.2) * mm});
            skLineSegment(sketch, "E371", {"start": v(-17.26, 6.2) * mm, "end": v(-17.26, 10.53) * mm});
            skLineSegment(sketch, "E372", {"start": v(-17.26, 10.53) * mm, "end": v(-19.05, 10.53) * mm});
            skLineSegment(sketch, "E373", {"start": v(-19.05, 10.53) * mm, "end": v(-19.05, 14.86) * mm});
            skLineSegment(sketch, "E374", {"start": v(-17.26, 14.86) * mm, "end": v(-19.05, 14.86) * mm});
            skLineSegment(sketch, "E375", {"start": v(-17.26, 14.86) * mm, "end": v(-17.26, 19.2) * mm});
            skLineSegment(sketch, "E376", {"start": v(-17.26, 19.2) * mm, "end": v(-19.05, 19.2) * mm});
            skLineSegment(sketch, "E377", {"start": v(-19.05, 19.2) * mm, "end": v(-19.05, 23.52) * mm});
            skLineSegment(sketch, "E378", {"start": v(-17.26, 23.52) * mm, "end": v(-19.05, 23.52) * mm});
            skLineSegment(sketch, "E379", {"start": v(-17.26, 23.52) * mm, "end": v(-17.26, 27.85) * mm});
            skLineSegment(sketch, "E380", {"start": v(-17.26, 27.85) * mm, "end": v(-19.05, 27.85) * mm});
            skLineSegment(sketch, "E381", {"start": v(-19.05, 27.85) * mm, "end": v(-19.05, 32.18) * mm});
            skLineSegment(sketch, "E382", {"start": v(-17.26, 32.18) * mm, "end": v(-19.05, 32.18) * mm});
            skLineSegment(sketch, "E383", {"start": v(-17.26, 32.18) * mm, "end": v(-17.26, 36.51) * mm});
            skLineSegment(sketch, "E384", {"start": v(-17.26, 36.51) * mm, "end": v(-19.05, 36.51) * mm});
            skLineSegment(sketch, "E385", {"start": v(-19.05, 36.51) * mm, "end": v(-19.05, 40.84) * mm});
            skLineSegment(sketch, "E386", {"start": v(-17.26, 40.84) * mm, "end": v(-19.05, 40.84) * mm});
            skLineSegment(sketch, "E387", {"start": v(-17.26, 40.84) * mm, "end": v(-17.26, 45.17) * mm});
            skLineSegment(sketch, "E388", {"start": v(-17.26, 45.17) * mm, "end": v(-19.05, 45.17) * mm});
            skLineSegment(sketch, "E389", {"start": v(-19.05, 45.17) * mm, "end": v(-19.05, 49.5) * mm});
            skLineSegment(sketch, "E390", {"start": v(17.26, 1.87) * mm, "end": v(17.26, 6.2) * mm});
            skLineSegment(sketch, "E391", {"start": v(19.05, 6.2) * mm, "end": v(17.26, 6.2) * mm});
            skLineSegment(sketch, "E392", {"start": v(19.05, 6.2) * mm, "end": v(19.05, 10.53) * mm});
            skLineSegment(sketch, "E393", {"start": v(19.05, 10.53) * mm, "end": v(17.26, 10.53) * mm});
            skLineSegment(sketch, "E394", {"start": v(17.26, 10.53) * mm, "end": v(17.26, 14.86) * mm});
            skLineSegment(sketch, "E395", {"start": v(19.05, 14.86) * mm, "end": v(17.26, 14.86) * mm});
            skLineSegment(sketch, "E396", {"start": v(19.05, 14.86) * mm, "end": v(19.05, 19.2) * mm});
            skLineSegment(sketch, "E397", {"start": v(19.05, 19.2) * mm, "end": v(17.26, 19.2) * mm});
            skLineSegment(sketch, "E398", {"start": v(17.26, 19.2) * mm, "end": v(17.26, 23.52) * mm});
            skLineSegment(sketch, "E399", {"start": v(19.05, 23.52) * mm, "end": v(17.26, 23.52) * mm});
            skLineSegment(sketch, "E400", {"start": v(19.05, 23.52) * mm, "end": v(19.05, 27.85) * mm});
            skLineSegment(sketch, "E401", {"start": v(19.05, 27.85) * mm, "end": v(17.26, 27.85) * mm});
            skLineSegment(sketch, "E402", {"start": v(17.26, 27.85) * mm, "end": v(17.26, 32.18) * mm});
            skLineSegment(sketch, "E403", {"start": v(19.05, 32.18) * mm, "end": v(17.26, 32.18) * mm});
            skLineSegment(sketch, "E404", {"start": v(19.05, 32.18) * mm, "end": v(19.05, 36.51) * mm});
            skLineSegment(sketch, "E405", {"start": v(19.05, 36.51) * mm, "end": v(17.26, 36.51) * mm});
            skLineSegment(sketch, "E406", {"start": v(17.26, 36.51) * mm, "end": v(17.26, 40.84) * mm});
            skLineSegment(sketch, "E407", {"start": v(19.05, 40.84) * mm, "end": v(17.26, 40.84) * mm});
            skLineSegment(sketch, "E408", {"start": v(19.05, 40.84) * mm, "end": v(19.05, 45.17) * mm});
            skLineSegment(sketch, "E409", {"start": v(19.05, 45.17) * mm, "end": v(17.26, 45.17) * mm});
            skLineSegment(sketch, "E410", {"start": v(17.26, 45.17) * mm, "end": v(17.26, 49.5) * mm});
            skLineSegment(sketch, "E411", {"start": v(-17.26, 55.04) * mm, "end": v(-14.82, 55.04) * mm});
            skLineSegment(sketch, "E412", {"start": v(-14.82, 55.04) * mm, "end": v(-14.82, 53.25) * mm});
            skLineSegment(sketch, "E413", {"start": v(-14.82, 53.25) * mm, "end": v(-10.58, 53.25) * mm});
            skLineSegment(sketch, "E414", {"start": v(-10.58, 55.04) * mm, "end": v(-10.58, 53.25) * mm});
            skLineSegment(sketch, "E415", {"start": v(-10.58, 55.04) * mm, "end": v(-6.35, 55.04) * mm});
            skLineSegment(sketch, "E416", {"start": v(-6.35, 55.04) * mm, "end": v(-6.35, 53.25) * mm});
            skLineSegment(sketch, "E417", {"start": v(-6.35, 53.25) * mm, "end": v(-2.12, 53.25) * mm});
            skLineSegment(sketch, "E418", {"start": v(-2.12, 55.04) * mm, "end": v(-2.12, 53.25) * mm});
            skLineSegment(sketch, "E419", {"start": v(-2.12, 55.04) * mm, "end": v(2.12, 55.04) * mm});
            skLineSegment(sketch, "E420", {"start": v(2.12, 55.04) * mm, "end": v(2.12, 53.25) * mm});
            skLineSegment(sketch, "E421", {"start": v(2.12, 53.25) * mm, "end": v(6.35, 53.25) * mm});
            skLineSegment(sketch, "E422", {"start": v(6.35, 55.04) * mm, "end": v(6.35, 53.25) * mm});
            skLineSegment(sketch, "E423", {"start": v(6.35, 55.04) * mm, "end": v(10.58, 55.04) * mm});
            skLineSegment(sketch, "E424", {"start": v(10.58, 55.04) * mm, "end": v(10.58, 53.25) * mm});
            skLineSegment(sketch, "E425", {"start": v(10.58, 53.25) * mm, "end": v(14.82, 53.25) * mm});
            skLineSegment(sketch, "E426", {"start": v(14.82, 55.04) * mm, "end": v(14.82, 53.25) * mm});
            skLineSegment(sketch, "E427", {"start": v(14.82, 55.04) * mm, "end": v(17.26, 55.04) * mm});
            skLineSegment(sketch, "E428", {"start": v(-17.26, 127.66) * mm, "end": v(-14.82, 127.66) * mm});
            skLineSegment(sketch, "E429", {"start": v(-14.82, 129.45) * mm, "end": v(-14.82, 127.66) * mm});
            skLineSegment(sketch, "E430", {"start": v(-14.82, 129.45) * mm, "end": v(-10.58, 129.45) * mm});
            skLineSegment(sketch, "E431", {"start": v(-10.58, 129.45) * mm, "end": v(-10.58, 127.66) * mm});
            skLineSegment(sketch, "E432", {"start": v(-10.58, 127.66) * mm, "end": v(-6.35, 127.66) * mm});
            skLineSegment(sketch, "E433", {"start": v(-6.35, 129.45) * mm, "end": v(-6.35, 127.66) * mm});
            skLineSegment(sketch, "E434", {"start": v(-6.35, 129.45) * mm, "end": v(-2.12, 129.45) * mm});
            skLineSegment(sketch, "E435", {"start": v(-2.12, 129.45) * mm, "end": v(-2.12, 127.66) * mm});
            skLineSegment(sketch, "E436", {"start": v(-2.12, 127.66) * mm, "end": v(2.12, 127.66) * mm});
            skLineSegment(sketch, "E437", {"start": v(2.12, 129.45) * mm, "end": v(2.12, 127.66) * mm});
            skLineSegment(sketch, "E438", {"start": v(2.12, 129.45) * mm, "end": v(6.35, 129.45) * mm});
            skLineSegment(sketch, "E439", {"start": v(6.35, 129.45) * mm, "end": v(6.35, 127.66) * mm});
            skLineSegment(sketch, "E440", {"start": v(6.35, 127.66) * mm, "end": v(10.58, 127.66) * mm});
            skLineSegment(sketch, "E441", {"start": v(10.58, 129.45) * mm, "end": v(10.58, 127.66) * mm});
            skLineSegment(sketch, "E442", {"start": v(10.58, 129.45) * mm, "end": v(14.82, 129.45) * mm});
            skLineSegment(sketch, "E443", {"start": v(14.82, 129.45) * mm, "end": v(14.82, 127.66) * mm});
            skLineSegment(sketch, "E444", {"start": v(14.82, 127.66) * mm, "end": v(17.26, 127.66) * mm});
            skLineSegment(sketch, "E445", {"start": v(-17.26, 55.04) * mm, "end": v(-17.26, 57.73) * mm});
            skLineSegment(sketch, "E446", {"start": v(-17.26, 57.73) * mm, "end": v(-19.05, 57.73) * mm});
            skLineSegment(sketch, "E447", {"start": v(-19.05, 57.73) * mm, "end": v(-19.05, 62.21) * mm});
            skLineSegment(sketch, "E448", {"start": v(-17.26, 62.21) * mm, "end": v(-19.05, 62.21) * mm});
            skLineSegment(sketch, "E449", {"start": v(-17.26, 62.21) * mm, "end": v(-17.26, 66.7) * mm});
            skLineSegment(sketch, "E450", {"start": v(-17.26, 66.7) * mm, "end": v(-19.05, 66.7) * mm});
            skLineSegment(sketch, "E451", {"start": v(-19.05, 66.7) * mm, "end": v(-19.05, 71.18) * mm});
            skLineSegment(sketch, "E452", {"start": v(-17.26, 71.18) * mm, "end": v(-19.05, 71.18) * mm});
            skLineSegment(sketch, "E453", {"start": v(-17.26, 71.18) * mm, "end": v(-17.26, 75.66) * mm});
            skLineSegment(sketch, "E454", {"start": v(-17.26, 75.66) * mm, "end": v(-19.05, 75.66) * mm});
            skLineSegment(sketch, "E455", {"start": v(-19.05, 75.66) * mm, "end": v(-19.05, 80.14) * mm});
            skLineSegment(sketch, "E456", {"start": v(-17.26, 80.14) * mm, "end": v(-19.05, 80.14) * mm});
            skLineSegment(sketch, "E457", {"start": v(-17.26, 80.14) * mm, "end": v(-17.26, 84.63) * mm});
            skLineSegment(sketch, "E458", {"start": v(-17.26, 84.63) * mm, "end": v(-19.05, 84.63) * mm});
            skLineSegment(sketch, "E459", {"start": v(-19.05, 84.63) * mm, "end": v(-19.05, 89.1) * mm});
            skLineSegment(sketch, "E460", {"start": v(-17.26, 89.1) * mm, "end": v(-19.05, 89.1) * mm});
            skLineSegment(sketch, "E461", {"start": v(-17.26, 89.1) * mm, "end": v(-17.26, 93.6) * mm});
            skLineSegment(sketch, "E462", {"start": v(-17.26, 93.6) * mm, "end": v(-19.05, 93.6) * mm});
            skLineSegment(sketch, "E463", {"start": v(-19.05, 93.6) * mm, "end": v(-19.05, 98.07) * mm});
            skLineSegment(sketch, "E464", {"start": v(-17.26, 98.07) * mm, "end": v(-19.05, 98.07) * mm});
            skLineSegment(sketch, "E465", {"start": v(-17.26, 98.07) * mm, "end": v(-17.26, 102.56) * mm});
            skLineSegment(sketch, "E466", {"start": v(-17.26, 102.56) * mm, "end": v(-19.05, 102.56) * mm});
            skLineSegment(sketch, "E467", {"start": v(-19.05, 102.56) * mm, "end": v(-19.05, 107.04) * mm});
            skLineSegment(sketch, "E468", {"start": v(-17.26, 107.04) * mm, "end": v(-19.05, 107.04) * mm});
            skLineSegment(sketch, "E469", {"start": v(-17.26, 107.04) * mm, "end": v(-17.26, 111.52) * mm});
            skLineSegment(sketch, "E470", {"start": v(-17.26, 111.52) * mm, "end": v(-19.05, 111.52) * mm});
            skLineSegment(sketch, "E471", {"start": v(-19.05, 111.52) * mm, "end": v(-19.05, 116) * mm});
            skLineSegment(sketch, "E472", {"start": v(-17.26, 116) * mm, "end": v(-19.05, 116) * mm});
            skLineSegment(sketch, "E473", {"start": v(-17.26, 116) * mm, "end": v(-17.26, 120.49) * mm});
            skLineSegment(sketch, "E474", {"start": v(-17.26, 120.49) * mm, "end": v(-19.05, 120.49) * mm});
            skLineSegment(sketch, "E475", {"start": v(-19.05, 120.49) * mm, "end": v(-19.05, 124.97) * mm});
            skLineSegment(sketch, "E476", {"start": v(-17.26, 124.97) * mm, "end": v(-19.05, 124.97) * mm});
            skLineSegment(sketch, "E477", {"start": v(-17.26, 124.97) * mm, "end": v(-17.26, 127.66) * mm});
            skLineSegment(sketch, "E478", {"start": v(17.26, 55.04) * mm, "end": v(17.26, 57.73) * mm});
            skLineSegment(sketch, "E479", {"start": v(19.05, 57.73) * mm, "end": v(17.26, 57.73) * mm});
            skLineSegment(sketch, "E480", {"start": v(19.05, 57.73) * mm, "end": v(19.05, 62.21) * mm});
            skLineSegment(sketch, "E481", {"start": v(19.05, 62.21) * mm, "end": v(17.26, 62.21) * mm});
            skLineSegment(sketch, "E482", {"start": v(17.26, 62.21) * mm, "end": v(17.26, 66.7) * mm});
            skLineSegment(sketch, "E483", {"start": v(19.05, 66.7) * mm, "end": v(17.26, 66.7) * mm});
            skLineSegment(sketch, "E484", {"start": v(19.05, 66.7) * mm, "end": v(19.05, 71.18) * mm});
            skLineSegment(sketch, "E485", {"start": v(19.05, 71.18) * mm, "end": v(17.26, 71.18) * mm});
            skLineSegment(sketch, "E486", {"start": v(17.26, 71.18) * mm, "end": v(17.26, 75.66) * mm});
            skLineSegment(sketch, "E487", {"start": v(19.05, 75.66) * mm, "end": v(17.26, 75.66) * mm});
            skLineSegment(sketch, "E488", {"start": v(19.05, 75.66) * mm, "end": v(19.05, 80.14) * mm});
            skLineSegment(sketch, "E489", {"start": v(19.05, 80.14) * mm, "end": v(17.26, 80.14) * mm});
            skLineSegment(sketch, "E490", {"start": v(17.26, 80.14) * mm, "end": v(17.26, 84.63) * mm});
            skLineSegment(sketch, "E491", {"start": v(19.05, 84.63) * mm, "end": v(17.26, 84.63) * mm});
            skLineSegment(sketch, "E492", {"start": v(19.05, 84.63) * mm, "end": v(19.05, 89.1) * mm});
            skLineSegment(sketch, "E493", {"start": v(19.05, 89.1) * mm, "end": v(17.26, 89.1) * mm});
            skLineSegment(sketch, "E494", {"start": v(17.26, 89.1) * mm, "end": v(17.26, 93.6) * mm});
            skLineSegment(sketch, "E495", {"start": v(19.05, 93.6) * mm, "end": v(17.26, 93.6) * mm});
            skLineSegment(sketch, "E496", {"start": v(19.05, 93.6) * mm, "end": v(19.05, 98.07) * mm});
            skLineSegment(sketch, "E497", {"start": v(19.05, 98.07) * mm, "end": v(17.26, 98.07) * mm});
            skLineSegment(sketch, "E498", {"start": v(17.26, 98.07) * mm, "end": v(17.26, 102.56) * mm});
            skLineSegment(sketch, "E499", {"start": v(19.05, 102.56) * mm, "end": v(17.26, 102.56) * mm});
            skLineSegment(sketch, "E500", {"start": v(19.05, 102.56) * mm, "end": v(19.05, 107.04) * mm});
            skLineSegment(sketch, "E501", {"start": v(19.05, 107.04) * mm, "end": v(17.26, 107.04) * mm});
            skLineSegment(sketch, "E502", {"start": v(17.26, 107.04) * mm, "end": v(17.26, 111.52) * mm});
            skLineSegment(sketch, "E503", {"start": v(19.05, 111.52) * mm, "end": v(17.26, 111.52) * mm});
            skLineSegment(sketch, "E504", {"start": v(19.05, 111.52) * mm, "end": v(19.05, 116) * mm});
            skLineSegment(sketch, "E505", {"start": v(19.05, 116) * mm, "end": v(17.26, 116) * mm});
            skLineSegment(sketch, "E506", {"start": v(17.26, 116) * mm, "end": v(17.26, 120.49) * mm});
            skLineSegment(sketch, "E507", {"start": v(19.05, 120.49) * mm, "end": v(17.26, 120.49) * mm});
            skLineSegment(sketch, "E508", {"start": v(19.05, 120.49) * mm, "end": v(19.05, 124.97) * mm});
            skLineSegment(sketch, "E509", {"start": v(19.05, 124.97) * mm, "end": v(17.26, 124.97) * mm});
            skLineSegment(sketch, "E510", {"start": v(17.26, 124.97) * mm, "end": v(17.26, 127.66) * mm});
            skLineSegment(sketch, "E511", {"start": v(-89.44, -71.2) * mm, "end": v(-88.17, -71.2) * mm});
            skLineSegment(sketch, "E512", {"start": v(-88.17, -37.32) * mm, "end": v(-89.44, -37.32) * mm});
            skLineSegment(sketch, "E513", {"start": v(-88.17, -71.2) * mm, "end": v(-88.17, -37.32) * mm});
            skLineSegment(sketch, "E514.trimOffspring", {"start": v(-89.44, -37.32) * mm, "end": v(-89.44, -71.2) * mm});
            skLineSegment(sketch, "E515.1.0.0", {"start": v(-81.82, -37.32) * mm, "end": v(-81.82, -71.2) * mm});
            skLineSegment(sketch, "E515.1.0.1", {"start": v(-80.55, -71.2) * mm, "end": v(-80.55, -37.32) * mm});
            skLineSegment(sketch, "E515.1.0.2", {"start": v(-80.55, -37.32) * mm, "end": v(-81.82, -37.32) * mm});
            skLineSegment(sketch, "E515.1.0.3", {"start": v(-81.82, -71.2) * mm, "end": v(-80.55, -71.2) * mm});
            skLineSegment(sketch, "E515.2.0.0", {"start": v(-74.2, -37.32) * mm, "end": v(-74.2, -71.2) * mm});
            skLineSegment(sketch, "E515.2.0.1", {"start": v(-72.93, -71.2) * mm, "end": v(-72.93, -37.32) * mm});
            skLineSegment(sketch, "E515.2.0.2", {"start": v(-72.93, -37.32) * mm, "end": v(-74.2, -37.32) * mm});
            skLineSegment(sketch, "E515.2.0.3", {"start": v(-74.2, -71.2) * mm, "end": v(-72.93, -71.2) * mm});
            skLineSegment(sketch, "E515.3.0.0", {"start": v(-66.58, -37.32) * mm, "end": v(-66.58, -71.2) * mm});
            skLineSegment(sketch, "E515.3.0.1", {"start": v(-65.3, -71.2) * mm, "end": v(-65.3, -37.32) * mm});
            skLineSegment(sketch, "E515.3.0.2", {"start": v(-65.3, -37.32) * mm, "end": v(-66.58, -37.32) * mm});
            skLineSegment(sketch, "E515.3.0.3", {"start": v(-66.58, -71.2) * mm, "end": v(-65.3, -71.2) * mm});
            skLineSegment(sketch, "E515.4.0.0", {"start": v(-58.96, -37.32) * mm, "end": v(-58.96, -71.2) * mm});
            skLineSegment(sketch, "E515.4.0.1", {"start": v(-57.69, -71.2) * mm, "end": v(-57.69, -37.32) * mm});
            skLineSegment(sketch, "E515.4.0.2", {"start": v(-57.69, -37.32) * mm, "end": v(-58.96, -37.32) * mm});
            skLineSegment(sketch, "E515.4.0.3", {"start": v(-58.96, -71.2) * mm, "end": v(-57.69, -71.2) * mm});
            skLineSegment(sketch, "E515.5.0.0", {"start": v(-51.34, -37.32) * mm, "end": v(-51.34, -71.2) * mm});
            skLineSegment(sketch, "E515.5.0.1", {"start": v(-50.07, -71.2) * mm, "end": v(-50.07, -37.32) * mm});
            skLineSegment(sketch, "E515.5.0.2", {"start": v(-50.07, -37.32) * mm, "end": v(-51.34, -37.32) * mm});
            skLineSegment(sketch, "E515.5.0.3", {"start": v(-51.34, -71.2) * mm, "end": v(-50.07, -71.2) * mm});
            skLineSegment(sketch, "E515.6.0.0", {"start": v(-43.72, -37.32) * mm, "end": v(-43.72, -71.2) * mm});
            skLineSegment(sketch, "E515.6.0.1", {"start": v(-42.45, -71.2) * mm, "end": v(-42.45, -37.32) * mm});
            skLineSegment(sketch, "E515.6.0.2", {"start": v(-42.45, -37.32) * mm, "end": v(-43.72, -37.32) * mm});
            skLineSegment(sketch, "E515.6.0.3", {"start": v(-43.72, -71.2) * mm, "end": v(-42.45, -71.2) * mm});
            skLineSegment(sketch, "E515.7.0.0", {"start": v(-36.1, -37.32) * mm, "end": v(-36.1, -71.2) * mm});
            skLineSegment(sketch, "E515.7.0.1", {"start": v(-34.83, -71.2) * mm, "end": v(-34.83, -37.32) * mm});
            skLineSegment(sketch, "E515.7.0.2", {"start": v(-34.83, -37.32) * mm, "end": v(-36.1, -37.32) * mm});
            skLineSegment(sketch, "E515.7.0.3", {"start": v(-36.1, -71.2) * mm, "end": v(-34.83, -71.2) * mm});
            skLineSegment(sketch, "E516.0", {"start": v(-85.63, -32.24) * mm, "end": v(-85.63, -50.02) * mm});
            skLineSegment(sketch, "E517.0", {"start": v(-84.36, -32.24) * mm, "end": v(-84.36, -50.02) * mm});
            skLineSegment(sketch, "E518.0", {"start": v(-85.63, -58.5) * mm, "end": v(-85.63, -76.29) * mm});
            skLineSegment(sketch, "E519.0", {"start": v(-84.36, -58.5) * mm, "end": v(-84.36, -76.29) * mm});
            skLineSegment(sketch, "E520", {"start": v(-85.63, -50.02) * mm, "end": v(-84.36, -50.02) * mm});
            skLineSegment(sketch, "E521", {"start": v(-84.36, -58.5) * mm, "end": v(-85.63, -58.5) * mm});
            skLineSegment(sketch, "E522.1.0.0", {"start": v(-76.74, -58.5) * mm, "end": v(-76.74, -76.29) * mm});
            skLineSegment(sketch, "E522.1.0.1", {"start": v(-78, -58.5) * mm, "end": v(-78, -76.29) * mm});
            skLineSegment(sketch, "E522.1.0.2", {"start": v(-76.74, -32.24) * mm, "end": v(-76.74, -50.02) * mm});
            skLineSegment(sketch, "E522.1.0.3", {"start": v(-78, -32.24) * mm, "end": v(-78, -50.02) * mm});
            skLineSegment(sketch, "E522.1.0.4", {"start": v(-76.74, -58.5) * mm, "end": v(-78, -58.5) * mm});
            skLineSegment(sketch, "E522.1.0.5", {"start": v(-78, -50.02) * mm, "end": v(-76.74, -50.02) * mm});
            skLineSegment(sketch, "E522.2.0.0", {"start": v(-69.12, -58.5) * mm, "end": v(-69.12, -76.29) * mm});
            skLineSegment(sketch, "E522.2.0.1", {"start": v(-70.39, -58.5) * mm, "end": v(-70.39, -76.29) * mm});
            skLineSegment(sketch, "E522.2.0.2", {"start": v(-69.12, -32.24) * mm, "end": v(-69.12, -50.02) * mm});
            skLineSegment(sketch, "E522.2.0.3", {"start": v(-70.39, -32.24) * mm, "end": v(-70.39, -50.02) * mm});
            skLineSegment(sketch, "E522.2.0.4", {"start": v(-69.12, -58.5) * mm, "end": v(-70.39, -58.5) * mm});
            skLineSegment(sketch, "E522.2.0.5", {"start": v(-70.39, -50.02) * mm, "end": v(-69.12, -50.02) * mm});
            skLineSegment(sketch, "E522.3.0.0", {"start": v(-61.5, -58.5) * mm, "end": v(-61.5, -76.29) * mm});
            skLineSegment(sketch, "E522.3.0.1", {"start": v(-62.77, -58.5) * mm, "end": v(-62.77, -76.29) * mm});
            skLineSegment(sketch, "E522.3.0.2", {"start": v(-61.5, -32.24) * mm, "end": v(-61.5, -50.02) * mm});
            skLineSegment(sketch, "E522.3.0.3", {"start": v(-62.77, -32.24) * mm, "end": v(-62.77, -50.02) * mm});
            skLineSegment(sketch, "E522.3.0.4", {"start": v(-61.5, -58.5) * mm, "end": v(-62.77, -58.5) * mm});
            skLineSegment(sketch, "E522.3.0.5", {"start": v(-62.77, -50.02) * mm, "end": v(-61.5, -50.02) * mm});
            skLineSegment(sketch, "E522.4.0.0", {"start": v(-53.88, -58.5) * mm, "end": v(-53.88, -76.29) * mm});
            skLineSegment(sketch, "E522.4.0.1", {"start": v(-55.15, -58.5) * mm, "end": v(-55.15, -76.29) * mm});
            skLineSegment(sketch, "E522.4.0.2", {"start": v(-53.88, -32.24) * mm, "end": v(-53.88, -50.02) * mm});
            skLineSegment(sketch, "E522.4.0.3", {"start": v(-55.15, -32.24) * mm, "end": v(-55.15, -50.02) * mm});
            skLineSegment(sketch, "E522.4.0.4", {"start": v(-53.88, -58.5) * mm, "end": v(-55.15, -58.5) * mm});
            skLineSegment(sketch, "E522.4.0.5", {"start": v(-55.15, -50.02) * mm, "end": v(-53.88, -50.02) * mm});
            skLineSegment(sketch, "E522.5.0.0", {"start": v(-46.26, -58.5) * mm, "end": v(-46.26, -76.29) * mm});
            skLineSegment(sketch, "E522.5.0.1", {"start": v(-47.53, -58.5) * mm, "end": v(-47.53, -76.29) * mm});
            skLineSegment(sketch, "E522.5.0.2", {"start": v(-46.26, -32.24) * mm, "end": v(-46.26, -50.02) * mm});
            skLineSegment(sketch, "E522.5.0.3", {"start": v(-47.53, -32.24) * mm, "end": v(-47.53, -50.02) * mm});
            skLineSegment(sketch, "E522.5.0.4", {"start": v(-46.26, -58.5) * mm, "end": v(-47.53, -58.5) * mm});
            skLineSegment(sketch, "E522.5.0.5", {"start": v(-47.53, -50.02) * mm, "end": v(-46.26, -50.02) * mm});
            skLineSegment(sketch, "E522.6.0.0", {"start": v(-38.64, -58.5) * mm, "end": v(-38.64, -76.29) * mm});
            skLineSegment(sketch, "E522.6.0.1", {"start": v(-39.9, -58.5) * mm, "end": v(-39.9, -76.29) * mm});
            skLineSegment(sketch, "E522.6.0.2", {"start": v(-38.64, -32.24) * mm, "end": v(-38.64, -50.02) * mm});
            skLineSegment(sketch, "E522.6.0.3", {"start": v(-39.9, -32.24) * mm, "end": v(-39.9, -50.02) * mm});
            skLineSegment(sketch, "E522.6.0.4", {"start": v(-38.64, -58.5) * mm, "end": v(-39.9, -58.5) * mm});
            skLineSegment(sketch, "E522.6.0.5", {"start": v(-39.9, -50.02) * mm, "end": v(-38.64, -50.02) * mm});
            skLineSegment(sketch, "E522.7.0.0", {"start": v(-31.02, -58.5) * mm, "end": v(-31.02, -76.29) * mm});
            skLineSegment(sketch, "E522.7.0.1", {"start": v(-32.29, -58.5) * mm, "end": v(-32.29, -76.29) * mm});
            skLineSegment(sketch, "E522.7.0.2", {"start": v(-31.02, -32.24) * mm, "end": v(-31.02, -50.02) * mm});
            skLineSegment(sketch, "E522.7.0.3", {"start": v(-32.29, -32.24) * mm, "end": v(-32.29, -50.02) * mm});
            skLineSegment(sketch, "E522.7.0.4", {"start": v(-31.02, -58.5) * mm, "end": v(-32.29, -58.5) * mm});
            skLineSegment(sketch, "E522.7.0.5", {"start": v(-32.29, -50.02) * mm, "end": v(-31.02, -50.02) * mm});
            skLineSegment(sketch, "E523.trimOffspring", {"start": v(-84.36, -32.24) * mm, "end": v(-78, -32.24) * mm});
            skLineSegment(sketch, "E524.trimOffspring", {"start": v(-69.12, -32.24) * mm, "end": v(-62.77, -32.24) * mm});
            skLineSegment(sketch, "E525.trimOffspring", {"start": v(-61.5, -32.24) * mm, "end": v(-55.15, -32.24) * mm});
            skLineSegment(sketch, "E526.trimOffspring", {"start": v(-53.88, -32.24) * mm, "end": v(-47.53, -32.24) * mm});
            skLineSegment(sketch, "E527.trimOffspring", {"start": v(-46.26, -32.24) * mm, "end": v(-39.9, -32.24) * mm});
            skLineSegment(sketch, "E528.trimOffspring", {"start": v(-38.64, -32.24) * mm, "end": v(-32.29, -32.24) * mm});
            skLineSegment(sketch, "E529.trimOffspring", {"start": v(-31.02, -32.24) * mm, "end": v(-27.28, -32.24) * mm});
            skLineSegment(sketch, "E530.trimOffspring", {"start": v(-31.02, -76.29) * mm, "end": v(-27.28, -76.29) * mm});
            skLineSegment(sketch, "E531.trimOffspring", {"start": v(-38.64, -76.29) * mm, "end": v(-32.29, -76.29) * mm});
            skLineSegment(sketch, "E532.trimOffspring", {"start": v(-46.26, -76.29) * mm, "end": v(-39.9, -76.29) * mm});
            skLineSegment(sketch, "E533.trimOffspring", {"start": v(-53.88, -76.29) * mm, "end": v(-47.53, -76.29) * mm});
            skLineSegment(sketch, "E534.trimOffspring", {"start": v(-61.5, -76.29) * mm, "end": v(-55.15, -76.29) * mm});
            skLineSegment(sketch, "E535.trimOffspring", {"start": v(-69.12, -76.29) * mm, "end": v(-62.77, -76.29) * mm});
            skLineSegment(sketch, "E536.trimOffspring", {"start": v(-76.74, -76.29) * mm, "end": v(-70.39, -76.29) * mm});
            skLineSegment(sketch, "E537", {"start": v(-76.74, -32.24) * mm, "end": v(-70.39, -32.24) * mm});
            skLineSegment(sketch, "E538", {"start": v(-85.63, -32.24) * mm, "end": v(-94.52, -32.24) * mm});
            skLineSegment(sketch, "E539.trimOffspring", {"start": v(-84.36, -76.29) * mm, "end": v(-78, -76.29) * mm});
            skSolve(sketch);
        }
        {
            var Q0;
            Q0=makeQuery(id+"F0.imprint","IMPRINT",FACE,{"disambiguationData":[TD([[makeQuery(id+"F0.imprint","IMPRINT",EDGE,{"derivedFrom":sQuery(id+"F0.wireOp",EDGE,"E411")}),1.0]])]});
            var Q1;
            Q1=makeQuery(id+"F0.imprint","IMPRINT",FACE,{"disambiguationData":[TD([[makeQuery(id+"F0.imprint","IMPRINT",EDGE,{"derivedFrom":sQuery(id+"F0.wireOp",EDGE,"E335")}),1.0]])]});
            var Q2;
            Q2=makeQuery(id+"F0.imprint","IMPRINT",FACE,{"disambiguationData":[TD([[makeQuery(id+"F0.imprint","IMPRINT",EDGE,{"derivedFrom":sQuery(id+"F0.wireOp",EDGE,"E127")}),1.0]])]});
            var Q3;
            Q3=makeQuery(id+"F0.imprint","IMPRINT",FACE,{"disambiguationData":[TD([[makeQuery(id+"F0.imprint","IMPRINT",EDGE,{"derivedFrom":sQuery(id+"F0.wireOp",EDGE,"E227")}),1.0]])]});
            var Q4;
            Q4=makeQuery(id+"F0.imprint","IMPRINT",FACE,{"disambiguationData":[TD([[makeQuery(id+"F0.imprint","IMPRINT",EDGE,{"derivedFrom":sQuery(id+"F0.wireOp",EDGE,"E0")}),1.0]])]});
            var Q5;
            Q5=makeQuery(id+"F0.imprint","IMPRINT",FACE,{"disambiguationData":[TD([[makeQuery(id+"F0.imprint","IMPRINT",EDGE,{"derivedFrom":sQuery(id+"F0.wireOp",EDGE,"E76")}),1.0]])]});
            extrude(context, id + "F1", {"entities" : qUnion([Q0, Q1, Q2, Q3, Q4, Q5]), "depth" : 5.08 * mm});
        }
    });
